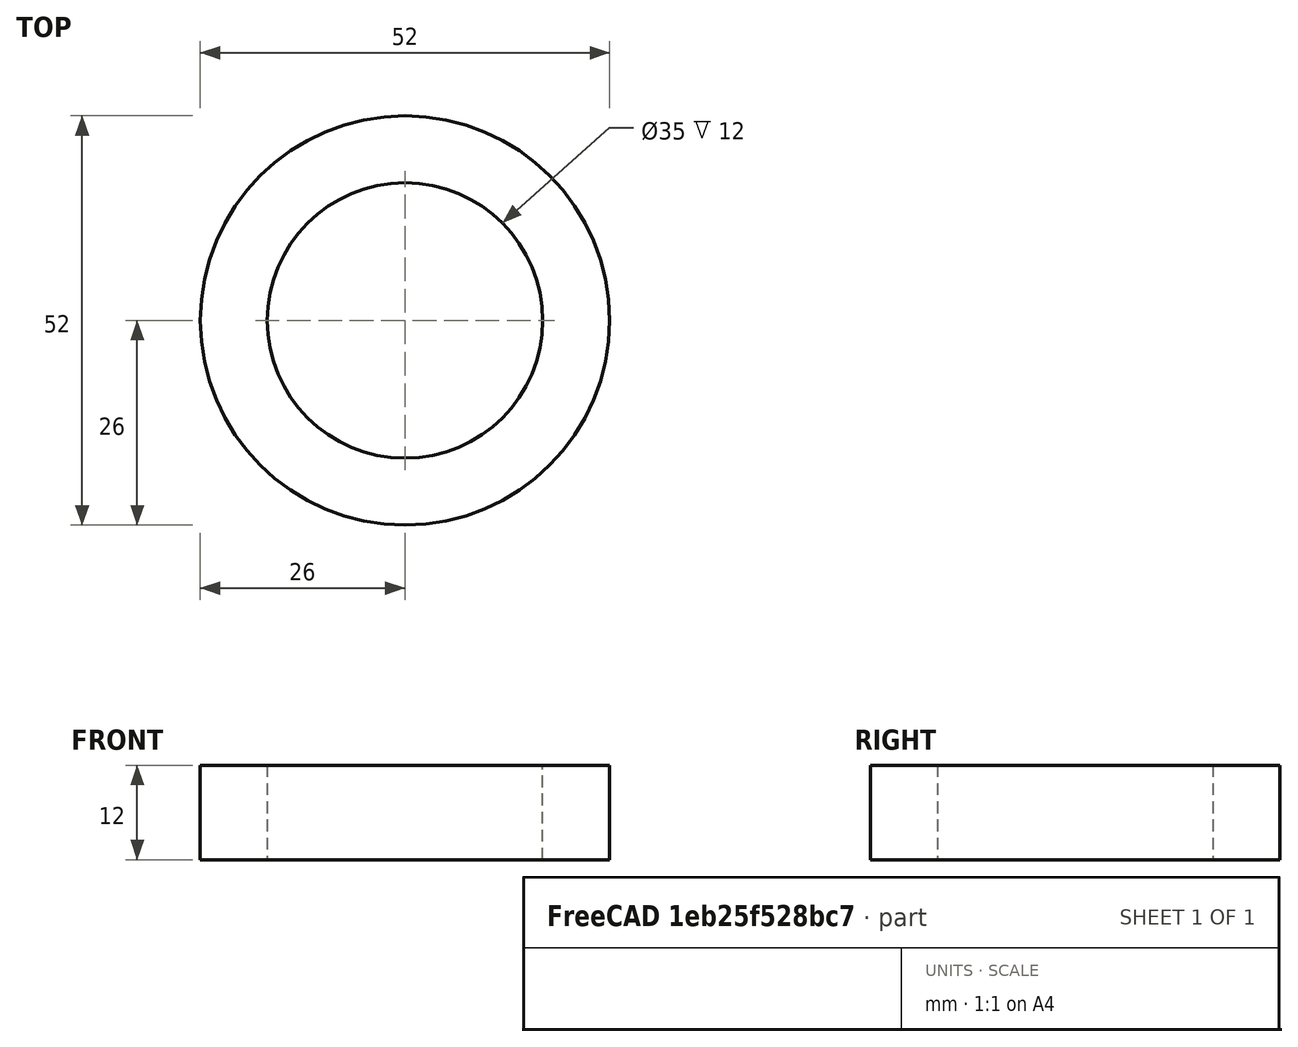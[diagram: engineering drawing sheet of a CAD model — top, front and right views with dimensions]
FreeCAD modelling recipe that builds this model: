
FCSTD DOCUMENT  (FreeCAD 0.21R33771 (Git))
Label: Reggispinta35x52x12
License: All rights reserved
LicenseURL: http://en.wikipedia.org/wiki/All_rights_reserved
objects: Sketcher::SketchObject×1, PartDesign::Pad×1, PartDesign::CoordinateSystem×1, PartDesign::Body×1
note: 5 computed .brp shape members not serialized (recipe doc carries the construction recipe); baked Part::Feature solids carry a one-line shape summary decoded from their .brp

FEATURE [Sketcher::SketchObject] Sketch
  FullyConstrained = true
  MapMode = 5
  Support = -> [XY_Plane]
  sketch-geometry (2):
    g0: Circle CenterX=0 CenterY=0 CenterZ=0 NormalX=0 NormalY=0 NormalZ=1 AngleXU=0 Radius=17.5
    g1: Circle CenterX=0 CenterY=0 CenterZ=0 NormalX=0 NormalY=0 NormalZ=1 AngleXU=0 Radius=26
  constraints (4):
    c: Coincident(g0,g-1)
    c: Radius(g0) = 17.5
    c: Coincident(g1,g0)
    c: Radius(g1) = 26
FEATURE [PartDesign::Pad] Pad
  Direction = (1,1,1)
  Length = 12
  Length2 = 100
  Profile = -> Sketch
  Type = 0
FEATURE [PartDesign::CoordinateSystem] LCS_Reggispinta35x12
  AttacherType = Attacher::AttachEngine3D
FEATURE [PartDesign::Body] Body
  Group = -> [Sketch,Pad,LCS_Reggispinta35x12]
  Origin = -> Origin
  Tip = -> Pad
